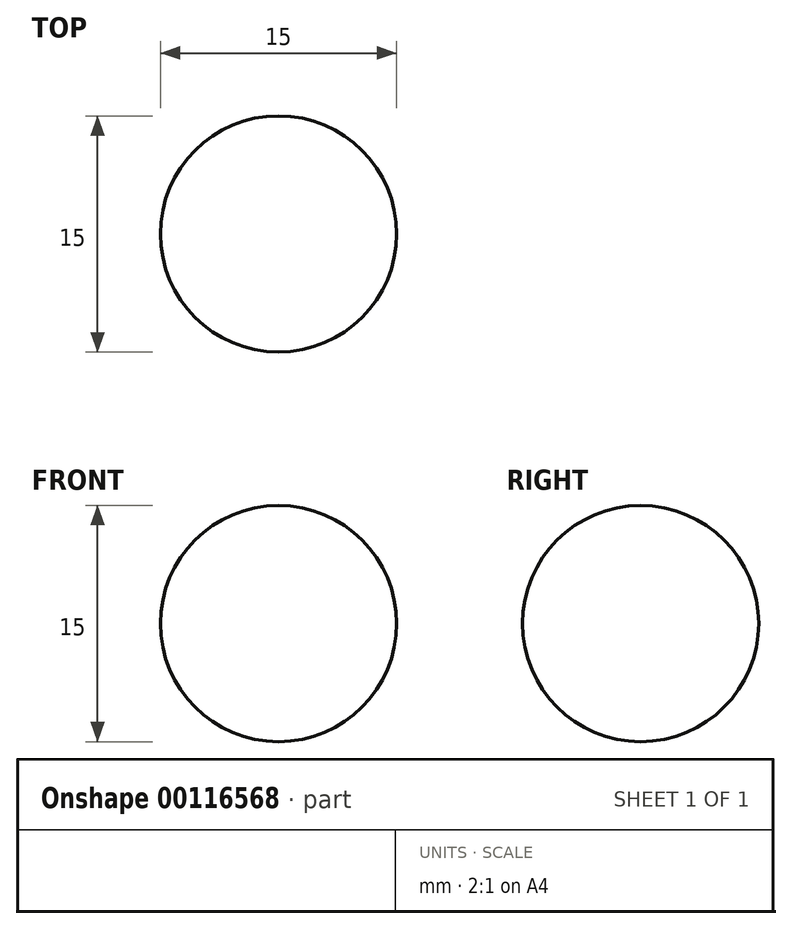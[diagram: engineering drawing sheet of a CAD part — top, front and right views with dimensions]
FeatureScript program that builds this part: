
annotation { "Feature Type Name" : "Feature", "Feature Type Description" : "" }
export const myFeature = defineFeature(function(context is Context, id is Id, definition is map)
    precondition{}
    {
        {
            var Q0;
            Q0=qCreatedBy(makeId("Top.planeOp"),FACE);
            var sketch = newSketch(context, id + "F0", { "sketchPlane" : qUnion([Q0])});
            skCircle(sketch, "E0", {"center": v(0, 0) * mm, "radius": 7.5 * mm});
            skSolve(sketch);
        }
        {
            var Q0;
            Q0=makeQuery(id+"F0.imprint","IMPRINT",FACE,{"disambiguationData":[TD([[makeQuery(id+"F0.imprint","IMPRINT",EDGE,{"derivedFrom":sQuery(id+"F0.wireOp",EDGE,"E0")}),1.0]])]});
            extrude(context, id + "F1", {"entities" : qUnion([Q0]), "endBound" : BoundingType.SYMMETRIC, "depth" : 15 * mm});
        }
        {
            var Q0;
            Q0=makeQuery(id+"F1.opExtrude","CAP_FACE",FACE,{"disambiguationData":[OSD([sQuery(id+"F0.wireOp",EDGE,"E0")])],"isStart":false});
            fillet(context, id + "F2", {"entities" : qUnion([Q0]), "radius" : 7.5 * mm, "tangentPropagation" : true, "allowEdgeOverflow" : false});
        }
        {
            var Q0;
            Q0=makeQuery(id+"F1.opExtrude","CAP_FACE",FACE,{"disambiguationData":[OSD([sQuery(id+"F0.wireOp",EDGE,"E0")])],"isStart":true});
            fillet(context, id + "F3", {"entities" : qUnion([Q0]), "radius" : 7.5 * mm, "tangentPropagation" : true, "allowEdgeOverflow" : false});
        }
    });
